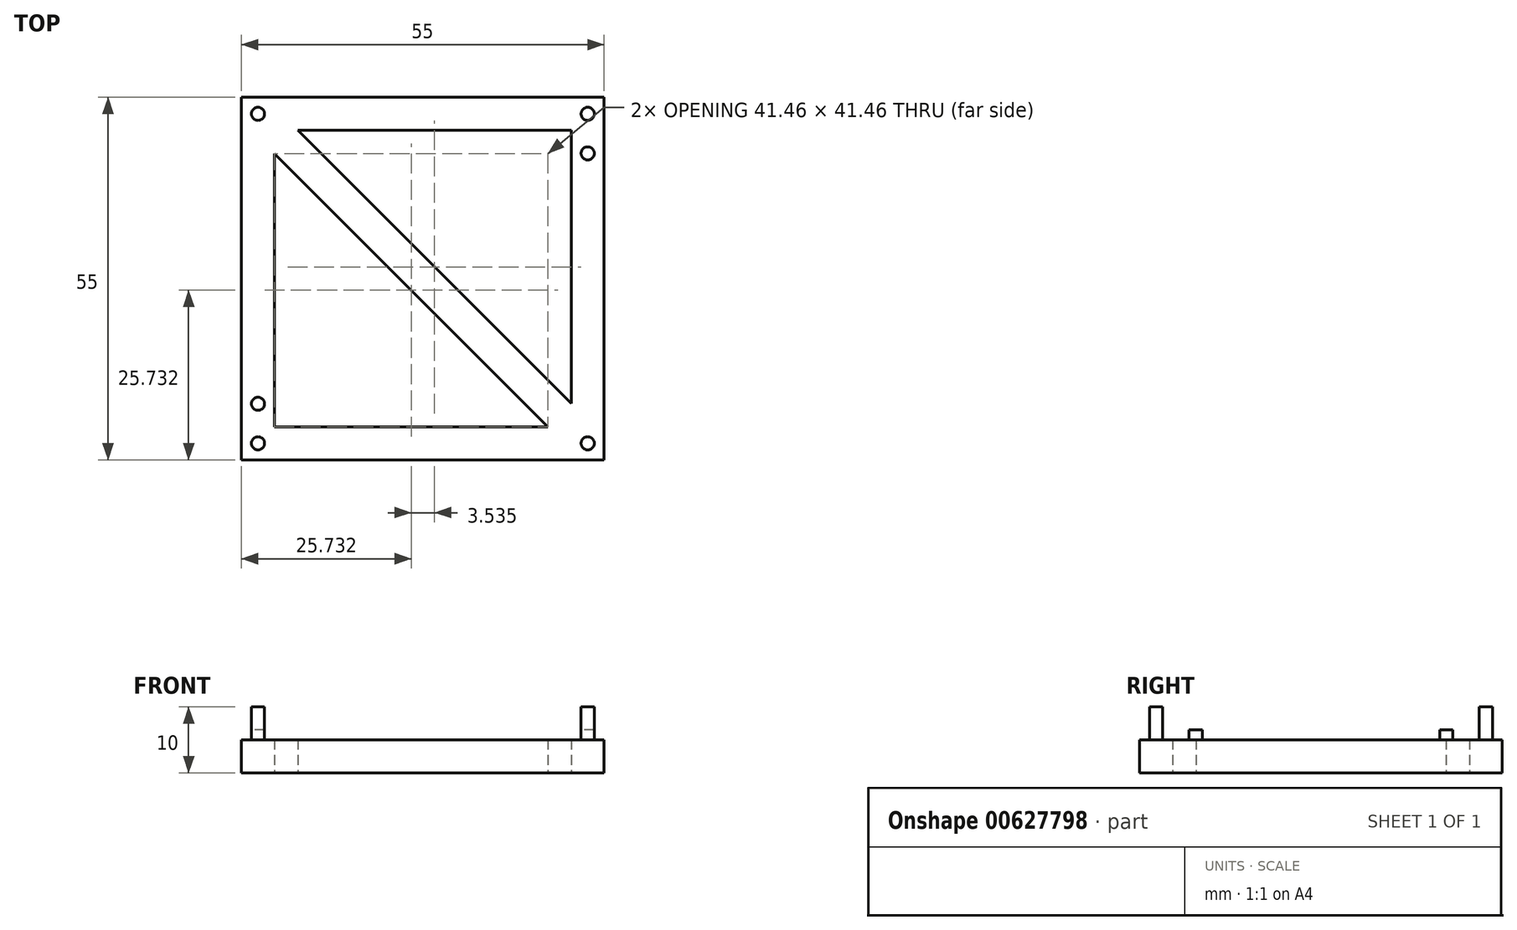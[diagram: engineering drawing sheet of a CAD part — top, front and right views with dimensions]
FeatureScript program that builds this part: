
annotation { "Feature Type Name" : "Feature", "Feature Type Description" : "" }
export const myFeature = defineFeature(function(context is Context, id is Id, definition is map)
    precondition{}
    {
        {
            var Q0;
            Q0=qCreatedBy(makeId("Top.planeOp"),FACE);
            var sketch = newSketch(context, id + "F0", { "sketchPlane" : qUnion([Q0])});
            skLineSegment(sketch, "E0.bottom", {"start": v(-27.5, -27.5) * mm, "end": v(27.5, -27.5) * mm});
            skLineSegment(sketch, "E0.top", {"start": v(-27.5, 27.5) * mm, "end": v(27.5, 27.5) * mm});
            skLineSegment(sketch, "E0.left", {"start": v(-27.5, -27.5) * mm, "end": v(-27.5, 27.5) * mm});
            skLineSegment(sketch, "E0.right", {"start": v(27.5, -27.5) * mm, "end": v(27.5, 27.5) * mm});
            skPoint(sketch, "E0.middle", {"position": v(0, 0) * mm});
            skLineSegment(sketch, "E1.0", {"start": v(-22.5, -22.5) * mm, "end": v(18.96, -22.5) * mm});
            skLineSegment(sketch, "E1.1", {"start": v(-22.5, -22.5) * mm, "end": v(-22.5, 18.96) * mm});
            skLineSegment(sketch, "E1.2", {"start": v(-18.96, 22.5) * mm, "end": v(22.5, 22.5) * mm});
            skLineSegment(sketch, "E1.3", {"start": v(22.5, -18.96) * mm, "end": v(22.5, 22.5) * mm});
            skLineSegment(sketch, "E2", {"start": v(-18.96, 22.5) * mm, "end": v(22.5, -18.96) * mm});
            skLineSegment(sketch, "E3", {"start": v(-22.5, 18.96) * mm, "end": v(18.96, -22.5) * mm});
            skSolve(sketch);
        }
        {
            var Q0;
            Q0=makeQuery(id+"F0.imprint","IMPRINT",FACE,{"disambiguationData":[TD([[makeQuery(id+"F0.imprint","IMPRINT",EDGE,{"derivedFrom":sQuery(id+"F0.wireOp",EDGE,"E0.bottom")}),1.0]])]});
            extrude(context, id + "F1", {"entities" : qUnion([Q0]), "depth" : 5 * mm, "offsetDistance" : 25 * mm});
        }
        {
            var Q0;
            Q0=makeQuery(id+"F1.opExtrude","CAP_FACE",FACE,{"disambiguationData":[OSD([sQuery(id+"F0.wireOp",EDGE,"E0.bottom"),sQuery(id+"F0.wireOp",EDGE,"E0.top"),sQuery(id+"F0.wireOp",EDGE,"E0.left"),sQuery(id+"F0.wireOp",EDGE,"E0.right"),sQuery(id+"F0.wireOp",EDGE,"E1.0"),sQuery(id+"F0.wireOp",EDGE,"E1.1"),sQuery(id+"F0.wireOp",EDGE,"E1.2"),sQuery(id+"F0.wireOp",EDGE,"E1.3"),sQuery(id+"F0.wireOp",EDGE,"E2"),sQuery(id+"F0.wireOp",EDGE,"E3")])],"isStart":false});
            var sketch = newSketch(context, id + "F2", { "sketchPlane" : qUnion([Q0])});
            skCircle(sketch, "E4", {"center": v(-25, 25) * mm, "radius": 1 * mm});
            skCircle(sketch, "E5", {"center": v(25, -25) * mm, "radius": 1 * mm});
            skCircle(sketch, "E6", {"center": v(25, 25) * mm, "radius": 1 * mm});
            skCircle(sketch, "E7", {"center": v(-25, -25) * mm, "radius": 1 * mm});
            skSolve(sketch);
        }
        {
            var Q0;
            Q0 = qSketchRegion(id + "F2", true);
            extrude(context, id + "F3", {"entities" : qUnion([Q0]), "operationType" : NewBodyOperationType.ADD, "depth" : 5 * mm, "offsetDistance" : 25 * mm});
        }
        {
            var Q0;
            Q0=makeQuery(id+"F1.opExtrude","CAP_FACE",FACE,{"disambiguationData":[OSD([sQuery(id+"F0.wireOp",EDGE,"E0.bottom"),sQuery(id+"F0.wireOp",EDGE,"E0.top"),sQuery(id+"F0.wireOp",EDGE,"E0.left"),sQuery(id+"F0.wireOp",EDGE,"E0.right"),sQuery(id+"F0.wireOp",EDGE,"E1.0"),sQuery(id+"F0.wireOp",EDGE,"E1.1"),sQuery(id+"F0.wireOp",EDGE,"E1.2"),sQuery(id+"F0.wireOp",EDGE,"E1.3"),sQuery(id+"F0.wireOp",EDGE,"E2"),sQuery(id+"F0.wireOp",EDGE,"E3")])],"isStart":false});
            var sketch = newSketch(context, id + "F4", { "sketchPlane" : qUnion([Q0])});
            skCircle(sketch, "E8", {"center": v(-25, -19) * mm, "radius": 1 * mm});
            skCircle(sketch, "E9", {"center": v(25, 19) * mm, "radius": 1 * mm});
            skSolve(sketch);
        }
        {
            var Q0;
            Q0 = qSketchRegion(id + "F4", true);
            extrude(context, id + "F5", {"entities" : qUnion([Q0]), "operationType" : NewBodyOperationType.ADD, "depth" : 1.5 * mm, "offsetDistance" : 25 * mm});
        }
    });
